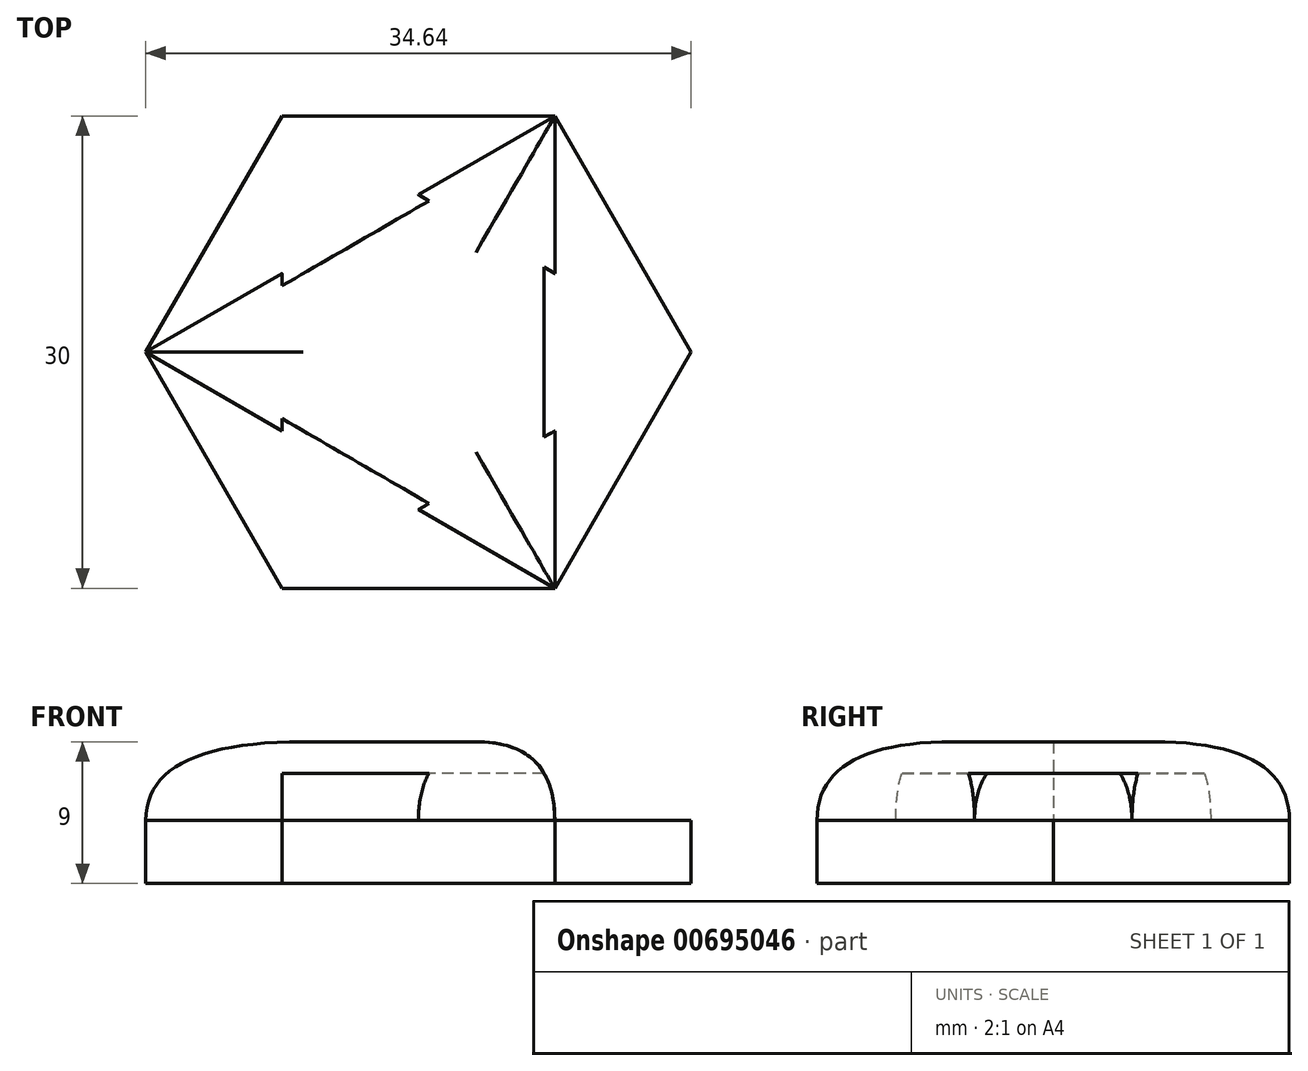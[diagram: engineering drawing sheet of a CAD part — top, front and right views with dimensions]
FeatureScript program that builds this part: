
annotation { "Feature Type Name" : "Feature", "Feature Type Description" : "" }
export const myFeature = defineFeature(function(context is Context, id is Id, definition is map)
    precondition{}
    {
        {
            var Q0;
            Q0=qCreatedBy(makeId("Top.planeOp"),FACE);
            var sketch = newSketch(context, id + "F0", { "sketchPlane" : qUnion([Q0])});
            skCircle(sketch, "E0.cCircle", {"center": v(0, 0) * mm, "radius": 15 * mm, "construction": true});
            skLineSegment(sketch, "E0.0", {"start": v(8.66, 15) * mm, "end": v(17.32, 0) * mm});
            skLineSegment(sketch, "E0.1", {"start": v(17.32, 0) * mm, "end": v(8.66, -15) * mm});
            skLineSegment(sketch, "E0.2", {"start": v(8.66, -15) * mm, "end": v(-8.66, -15) * mm});
            skLineSegment(sketch, "E0.3", {"start": v(-8.66, -15) * mm, "end": v(-17.32, 0) * mm});
            skLineSegment(sketch, "E0.4", {"start": v(-17.32, 0) * mm, "end": v(-8.66, 15) * mm});
            skLineSegment(sketch, "E0.5", {"start": v(-8.66, 15) * mm, "end": v(8.66, 15) * mm});
            skPoint(sketch, "E0.0.midPoint", {"position": v(13, 7.5) * mm});
            skSolve(sketch);
        }
        {
            var Q0;
            Q0 = qSketchRegion(id + "F0", true);
            extrude(context, id + "F1", {"entities" : qUnion([Q0]), "depth" : 4 * mm, "offsetDistance" : 25 * mm});
        }
        {
            var Q0;
            Q0=makeQuery(id+"F1.opExtrude","CAP_FACE",FACE,{"disambiguationData":[OSD([sQuery(id+"F0.wireOp",EDGE,"E0.0"),sQuery(id+"F0.wireOp",EDGE,"E0.1"),sQuery(id+"F0.wireOp",EDGE,"E0.2"),sQuery(id+"F0.wireOp",EDGE,"E0.3"),sQuery(id+"F0.wireOp",EDGE,"E0.4"),sQuery(id+"F0.wireOp",EDGE,"E0.5")])],"isStart":false});
            var sketch = newSketch(context, id + "F2", { "sketchPlane" : qUnion([Q0])});
            skCircle(sketch, "E1.cCircle", {"center": v(0, 0) * mm, "radius": 8.66 * mm, "construction": true});
            skLineSegment(sketch, "E1.0", {"start": v(8.66, 15) * mm, "end": v(8.66, -15) * mm});
            skLineSegment(sketch, "E1.1", {"start": v(8.66, -15) * mm, "end": v(-17.32, 0) * mm});
            skLineSegment(sketch, "E1.2", {"start": v(-17.32, 0) * mm, "end": v(8.66, 15) * mm});
            skPoint(sketch, "E1.0.midPoint", {"position": v(8.66, 0) * mm});
            skSolve(sketch);
        }
        {
            var Q0;
            Q0 = qSketchRegion(id + "F2", true);
            extrude(context, id + "F3", {"entities" : qUnion([Q0]), "operationType" : NewBodyOperationType.ADD, "depth" : 5 * mm, "offsetDistance" : 25 * mm});
        }
        {
            var Q0;
            Q0=makeQuery(id+"F2.imprint","IMPRINT",FACE,{"disambiguationData":[TD([[makeQuery(id+"F2.imprint","IMPRINT",EDGE,{"derivedFrom":sQuery(id+"F2.wireOp",EDGE,"E1.1")}),1.0]])]});
            var sketch = newSketch(context, id + "F4", { "sketchPlane" : qUnion([Q0]), "disableImprinting" : false});
            skCircle(sketch, "E2.cCircle", {"center": v(0, 0) * mm, "radius": 8.66 * mm, "construction": true});
            skLineSegment(sketch, "E2.0", {"start": v(8.66, 5) * mm, "end": v(8.66, -5) * mm});
            skLineSegment(sketch, "E2.1", {"start": v(8.66, -5) * mm, "end": v(0, -10) * mm});
            skLineSegment(sketch, "E2.2", {"start": v(0, -10) * mm, "end": v(-8.66, -5) * mm});
            skLineSegment(sketch, "E2.3", {"start": v(-8.66, -5) * mm, "end": v(-8.66, 5) * mm});
            skLineSegment(sketch, "E2.4", {"start": v(-8.66, 5) * mm, "end": v(0, 10) * mm});
            skLineSegment(sketch, "E2.5", {"start": v(0, 10) * mm, "end": v(8.66, 5) * mm});
            skPoint(sketch, "E2.0.midPoint", {"position": v(8.66, 0) * mm});
            skSolve(sketch);
        }
        {
            var Q0;
            Q0 = qSketchRegion(id + "F4", true);
            extrude(context, id + "F5", {"entities" : qUnion([Q0]), "operationType" : NewBodyOperationType.REMOVE, "depth" : 3 * mm, "offsetDistance" : 25 * mm});
        }
        {
            var Q0;
            Q0=makeQuery(id+"F3.opExtrude","CAP_EDGE",EDGE,{"disambiguationData":[OSD([sQuery(id+"F2.wireOp",EDGE,"E1.1")])],"isStart":false});
            var Q1;
            Q1=makeQuery(id+"F3.opExtrude","CAP_EDGE",EDGE,{"disambiguationData":[OSD([sQuery(id+"F2.wireOp",EDGE,"E1.0")])],"isStart":false});
            var Q2;
            Q2=makeQuery(id+"F3.opExtrude","CAP_EDGE",EDGE,{"disambiguationData":[OSD([sQuery(id+"F2.wireOp",EDGE,"E1.2")])],"isStart":false});
            fillet(context, id + "F6", {"entities" : qUnion([Q0, Q1, Q2]), "radius" : 5 * mm, "tangentPropagation" : true, "rho" : 0.5, "crossSection" : FilletCrossSection.CONIC, "allowEdgeOverflow" : false});
        }
    });
